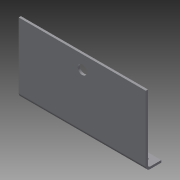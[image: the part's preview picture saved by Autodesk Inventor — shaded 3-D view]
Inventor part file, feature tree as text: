
AUTODESK INVENTOR PART (.ipt)
format: ipt  version: 2014 (Build 180170000, 170)  size: 125,952 bytes
history: native  units: in
note: dims shown in document units (in); Inventor stores cm internally (conversion verified against a paired STEP export)
features: sheet_metal_op x2, other x2, sketch x1
ambient origin geometry x8: Origin, YZ Plane, XZ Plane, XY Plane, X Axis, Y Axis, Z Axis, Center Point
bodies: Solid1 (feature_tree)
feature tree (5):
  sketch  "Sketch1"  dims[d0=7.0in d1=4.5in d2=0.375in d3=0.5in d4=0.375in d5=0.5in d7=0.25in d8=0.25in d9=0.5in d10=0.75in d11=3.0in d12=0.12in d13=0.12in d14=0.06in d15=0.24in d16=0.12in d17=90.0deg d18=0.12in]
  sheet_metal_op  "Face1"
  sheet_metal_op  "Fold1"
  other  "Plate1"
  other  "Definition1"
